# Revit family: Lighting-Recessed-Luminii-Minimo_Pro_Intl
name_source: partatom
category: Lighting Fixtures
units: mm (PartAtom-declared; Revit-internal decimal feet)

## family parameters
Cut with Voids When Loaded = No
Host = Face
Light Source = No
OmniClass Number = 23.80.70.11.14.11
OmniClass Title = Downlights
Part Type = Normal
Room Calculation Point = No
Round Connector Dimension = Use Diameter
Shared = No

## types (1)
- Custom
    Aperture Finish = Metal - Luminii - Black
    Apparent Load = 12 VA
    Assembly Code = D5020200
    Default Elevation = 48"
    Description = ADJUSTABLE RECESSED DOWNLIGHT
    Input Wattage = 12 W
    Keynote = 16510
    Lamp = LED
    Lens Finish = Acrylic - Luminii - White
    Light Engine Finish = Metal - Luminii - Black
    Manufacturer = LUMINII
    Model = MINIMO PRO
    Trim Finish = Metal - Luminii - White
    URL = https://www.luminii.com
    Voltage = 120 V

## geometry (parser evidence)
native form markers: Sweep x6
no freeform markers — native parametric forms only
